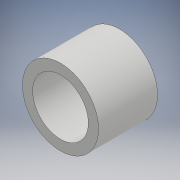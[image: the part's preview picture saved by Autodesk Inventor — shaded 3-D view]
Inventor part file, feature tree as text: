
AUTODESK INVENTOR PART (.ipt)
format: ipt  version: 2018 (Build 220112000, 112)  size: 98,816 bytes
history: native  units: mm
features: extrude x1, sketch x1
ambient origin geometry x8: Origin, YZ Plane, XZ Plane, XY Plane, X Axis, Y Axis, Z Axis, Center Point
bodies: Solid1 (feature_tree)
feature tree (2):
  extrude  "Extrusion1"  Depth=3.18mm
  sketch  "Sketch1"  dims[d0=4.1mm d1=3.0mm d2=3.18mm d3=0.0mm]
